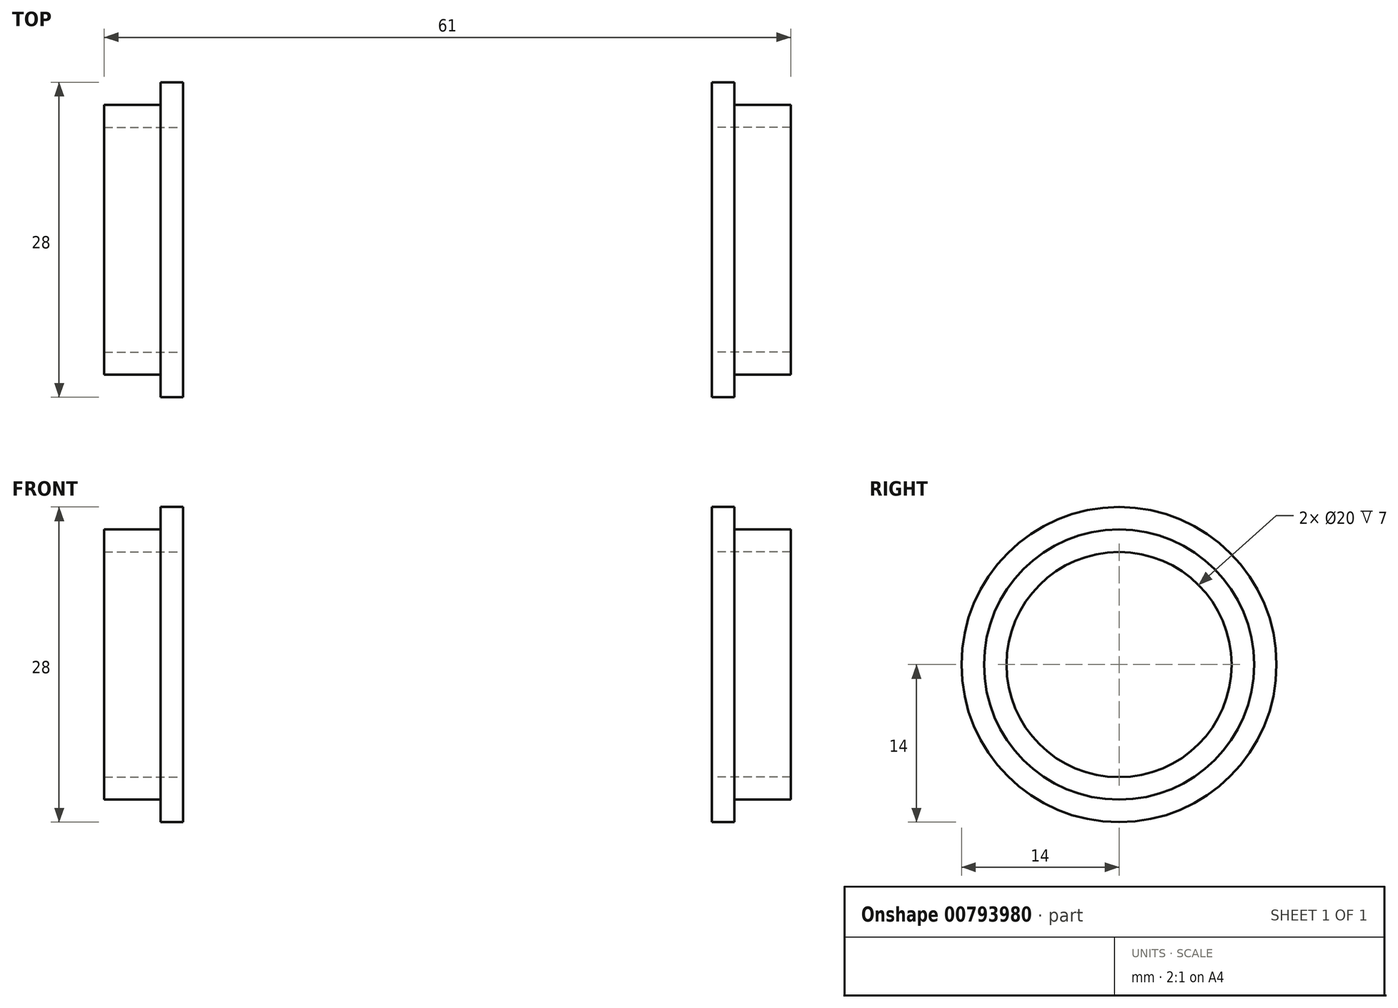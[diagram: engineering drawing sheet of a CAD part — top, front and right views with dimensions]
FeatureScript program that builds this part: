
annotation { "Feature Type Name" : "Feature", "Feature Type Description" : "" }
export const myFeature = defineFeature(function(context is Context, id is Id, definition is map)
    precondition{}
    {
        {
            var Q0;
            Q0=qCreatedBy(makeId("Right.planeOp"),FACE);
            var sketch = newSketch(context, id + "F0", { "sketchPlane" : qUnion([Q0])});
            skCircle(sketch, "E0", {"center": v(0, 0) * mm, "radius": 10 * mm});
            skCircle(sketch, "E1", {"center": v(0, 0) * mm, "radius": 12 * mm});
            skCircle(sketch, "E2", {"center": v(0, 0) * mm, "radius": 14 * mm});
            skSolve(sketch);
        }
        {
            var Q0;
            Q0=makeQuery(id+"F0.imprint","IMPRINT",FACE,{"disambiguationData":[TD([[makeQuery(id+"F0.imprint","IMPRINT",EDGE,{"derivedFrom":sQuery(id+"F0.wireOp",EDGE,"E0")}),-1.0]])]});
            extrude(context, id + "F1", {"entities" : qUnion([Q0]), "depth" : 7 * mm, "offsetDistance" : 25 * mm});
        }
        {
            var Q0;
            Q0=makeQuery(id+"F0.imprint","IMPRINT",FACE,{"disambiguationData":[TD([[makeQuery(id+"F0.imprint","IMPRINT",EDGE,{"derivedFrom":sQuery(id+"F0.wireOp",EDGE,"E1")}),-1.0]])]});
            extrude(context, id + "F2", {"entities" : qUnion([Q0]), "operationType" : NewBodyOperationType.ADD, "depth" : 2 * mm, "offsetDistance" : 25 * mm});
        }
        {
            var Q0;
            Q0=qCreatedBy(makeId("Right.planeOp"),FACE);
            cPlane(context, id + "F3", {"entities" : qUnion([Q0]), "cplaneType" : CPlaneType.OFFSET, "offset" : (47 / 2) * mm, "oppositeDirection" : true, "width" : 150 * mm, "height" : 150 * mm});
        }
        {
            var Q0;
            Q0=makeQuery(id+"F1.opExtrude","SWEPT_BODY",BODY,{"disambiguationData":[OSD([sQuery(id+"F0.wireOp",EDGE,"E0"),sQuery(id+"F0.wireOp",EDGE,"E1")])]});
            var Q1;
            Q1=qCreatedBy(id+"F3.planeOp",FACE);
            mirror(context, id + "F4", {"entities" : qUnion([Q0]), "mirrorPlane" : qUnion([Q1])});
        }
    });
